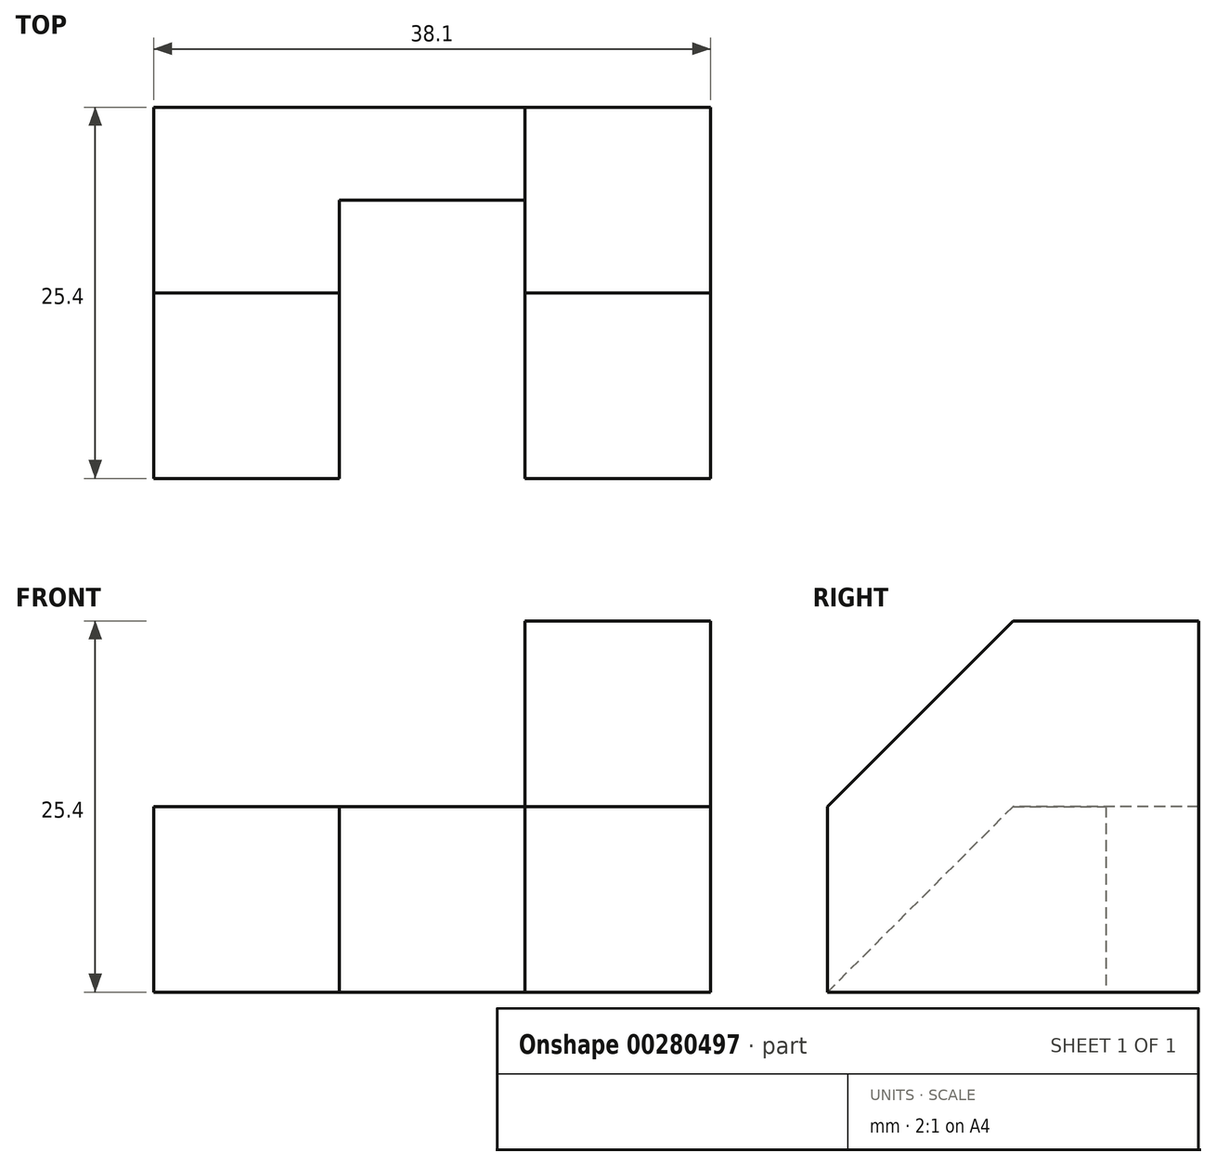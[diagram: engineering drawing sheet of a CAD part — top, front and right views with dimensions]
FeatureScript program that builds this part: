
annotation { "Feature Type Name" : "Feature", "Feature Type Description" : "" }
export const myFeature = defineFeature(function(context is Context, id is Id, definition is map)
    precondition{}
    {
        {
            var Q0;
            Q0=qCreatedBy(makeId("Front.planeOp"),FACE);
            var sketch = newSketch(context, id + "F0", { "sketchPlane" : qUnion([Q0])});
            skLineSegment(sketch, "E0", {"start": v(-19.05, 0) * mm, "end": v(19.05, 0) * mm});
            skLineSegment(sketch, "E1", {"start": v(19.05, 0) * mm, "end": v(19.05, 25.4) * mm});
            skLineSegment(sketch, "E2", {"start": v(19.05, 25.4) * mm, "end": v(6.35, 25.4) * mm});
            skLineSegment(sketch, "E3", {"start": v(6.35, 25.4) * mm, "end": v(6.35, 12.7) * mm});
            skLineSegment(sketch, "E4", {"start": v(6.35, 12.7) * mm, "end": v(-6.35, 12.7) * mm});
            skLineSegment(sketch, "E5", {"start": v(-6.35, 12.7) * mm, "end": v(-19.05, 12.7) * mm});
            skLineSegment(sketch, "E6", {"start": v(-19.05, 12.7) * mm, "end": v(-19.05, 0) * mm});
            skLineSegment(sketch, "E7", {"start": v(-6.35, 12.7) * mm, "end": v(-6.35, 0) * mm});
            skLineSegment(sketch, "E8", {"start": v(6.35, 12.7) * mm, "end": v(6.35, 0) * mm});
            skSolve(sketch);
        }
        {
            var Q0;
            Q0=makeQuery(id+"F0.imprint","IMPRINT",FACE,{"disambiguationData":[TD([[makeQuery(id+"F0.imprint","IMPRINT",EDGE,{"derivedFrom":sQuery(id+"F0.wireOp",EDGE,"E5")}),1.0]])]});
            var Q1;
            {var subQ0=sQuery(id+"F0.wireOp",EDGE,"E1");Q1=makeQuery(id+"F0.imprint","IMPRINT",FACE,{"disambiguationData":[TD([[makeQuery(id+"F0.imprint","IMPRINT",EDGE,{"derivedFrom":subQ0}),1.0]])]});}
            var Q2;
            Q2=makeQuery(id+"F0.imprint","IMPRINT",FACE,{"disambiguationData":[TD([[makeQuery(id+"F0.imprint","IMPRINT",EDGE,{"derivedFrom":sQuery(id+"F0.wireOp",EDGE,"E4")}),1.0]])]});
            extrude(context, id + "F1", {"entities" : qUnion([Q0, Q1, Q2]), "oppositeDirection" : true, "depth" : 6.35 * mm});
        }
        {
            var Q0;
            Q0=makeQuery(id+"F0.imprint","IMPRINT",FACE,{"disambiguationData":[TD([[makeQuery(id+"F0.imprint","IMPRINT",EDGE,{"derivedFrom":sQuery(id+"F0.wireOp",EDGE,"E5")}),1.0]])]});
            var Q1;
            {var subQ0=sQuery(id+"F0.wireOp",EDGE,"E1");Q1=makeQuery(id+"F0.imprint","IMPRINT",FACE,{"disambiguationData":[TD([[makeQuery(id+"F0.imprint","IMPRINT",EDGE,{"derivedFrom":subQ0}),1.0]])]});}
            extrude(context, id + "F2", {"entities" : qUnion([Q0, Q1]), "operationType" : NewBodyOperationType.ADD, "depth" : 19.05 * mm});
        }
        {
            var Q0;
            {var subQ0=sQuery(id+"F0.wireOp",EDGE,"E1");Q0=makeQuery(id+"F2.boolean.opBoolean","MERGE",FACE,{"derivedFrom":[makeQuery(id+"F1.opExtrude","SWEPT_FACE",FACE,{"disambiguationData":[OSD([subQ0])]}),makeQuery(id+"F2.opExtrude","SWEPT_FACE",FACE,{"disambiguationData":[OSD([subQ0])]})]});}
            var sketch = newSketch(context, id + "F3", { "sketchPlane" : qUnion([Q0])});
            skLineSegment(sketch, "E9", {"start": v(-19.05, 12.7) * mm, "end": v(-6.35, 25.4) * mm});
            skLineSegment(sketch, "E10", {"start": v(-6.35, 25.4) * mm, "end": v(-19.05, 25.4) * mm});
            skLineSegment(sketch, "E11", {"start": v(-19.05, 25.4) * mm, "end": v(-19.05, 12.7) * mm});
            skSolve(sketch);
        }
        {
            var Q0;
            Q0=makeQuery(id+"F2.opExtrude","SWEPT_FACE",FACE,{"disambiguationData":[OSD([sQuery(id+"F0.wireOp",EDGE,"E7")])]});
            var sketch = newSketch(context, id + "F4", { "sketchPlane" : qUnion([Q0])});
            skLineSegment(sketch, "E12", {"start": v(-19.05, 0) * mm, "end": v(-6.35, 12.7) * mm});
            skLineSegment(sketch, "E13", {"start": v(-6.35, 12.7) * mm, "end": v(-19.05, 12.7) * mm});
            skLineSegment(sketch, "E14", {"start": v(-19.05, 12.7) * mm, "end": v(-19.05, 0) * mm});
            skSolve(sketch);
        }
        {
            var Q0;
            Q0=makeQuery(id+"F4.imprint","IMPRINT",FACE,{"disambiguationData":[TD([[makeQuery(id+"F4.imprint","IMPRINT",EDGE,{"derivedFrom":sQuery(id+"F4.wireOp",EDGE,"E12")}),1.0]])]});
            var Q1;
            Q1=makeQuery(id+"F3.imprint","IMPRINT",FACE,{"disambiguationData":[TD([[makeQuery(id+"F3.imprint","IMPRINT",EDGE,{"derivedFrom":sQuery(id+"F3.wireOp",EDGE,"E9")}),1.0]])]});
            extrude(context, id + "F5", {"entities" : qUnion([Q0, Q1]), "operationType" : NewBodyOperationType.REMOVE, "endBound" : BoundingType.THROUGH_ALL, "oppositeDirection" : true, "depth" : 25.4 * mm});
        }
    });
